# Revit family: VLGFP1501-xxxSIxx0Wxxxx
name_source: partatom
category: Oprawy oświetleniowe
revit_build: Autodesk Revit 2017 (Build: 20190508_0315(x64)
units: mm (PartAtom-declared; Revit-internal decimal feet)

## family parameters
Numer OmniClass = 23.80.70.11
Obiekt nadrzędny = Powierzchnia
Punkt obliczania pomieszczeń = Nie
Tnij formami wycięć po wczytaniu = Nie
Typ części = Normalny
Tytuł OmniClass = Luminaries for Internal Lighting
Współdzielony = Nie
Wymiar okrągłego złącza = Użyj średnicy
Źródło światła = Tak

## types (8) — shared parameters
Emituj kształt widoczny w renderingu = Nie
Emituj z długości prostokąta = 63 mm  [stored 0.206693 ft]
Emituj z szerokości prostokąta = 1463 mm  [stored 4.79987 ft]
Filtr koloru = 16777215
Kod zespołu = D5020200
Lampa = LED
Odchylenie kierunku = 90.00°
Plik sieci fotometrycznej = VLGFP1501-5NDWS840W0800.IES
Producent = RIDI Leuchten GmbH
URL = www.ridi.de
Zmiana temperatury barwowej przyciemniania lampy = <Brak>
brand = RIDI
conformity mark = CE
electrical safety class = 1
height = 66 mm  [stored 0.216535 ft]
ingress protection (IP) code = IP40
length = 1500 mm  [stored 4.92126 ft]
nominal frequency = 50-60Hz
nominal voltage = 230
voltage type (AC, DC, UC) = AC
weight = 2.19 kg
width = 67 mm
zero-valued in all types: Domyślna rzędna

## per-type parameters (varying)
| type | Model | Obciążenie pozorne | rated input power |
| VLGFP1501-7DASI830W0750 | 1561171SI | 55 VA | 55 |
| VLGFP1501-5NDSI830W0750-RF | 1551212SI | 58 VA | 58 |
| VLGFP1501-7DASI840W0800 | 1561172SI | 55 VA | 55 |
| VLGFP1501-7DASI840W0800-RF | 1551213SI | 58 VA | 58 |
| VLGFP1501-7DASI850W0800 | 1561173SI | 55 VA | 55 |
| VLGFP1501-5NDSI850W0800-RF | 1551214SI | 58 VA | 58 |
| VLGFP1501-7DASI865W0800 | 1561174SI | 55 VA | 55 |
| VLGFP1501-5NDSI865W0800-RF | 1551215SI | 58 VA | 58 |

note: column(s) folded — value = type name in every type: product name

note: [stored X ft] marks values corroborated as IEEE doubles in the binary element streams (Revit-internal decimal feet)
